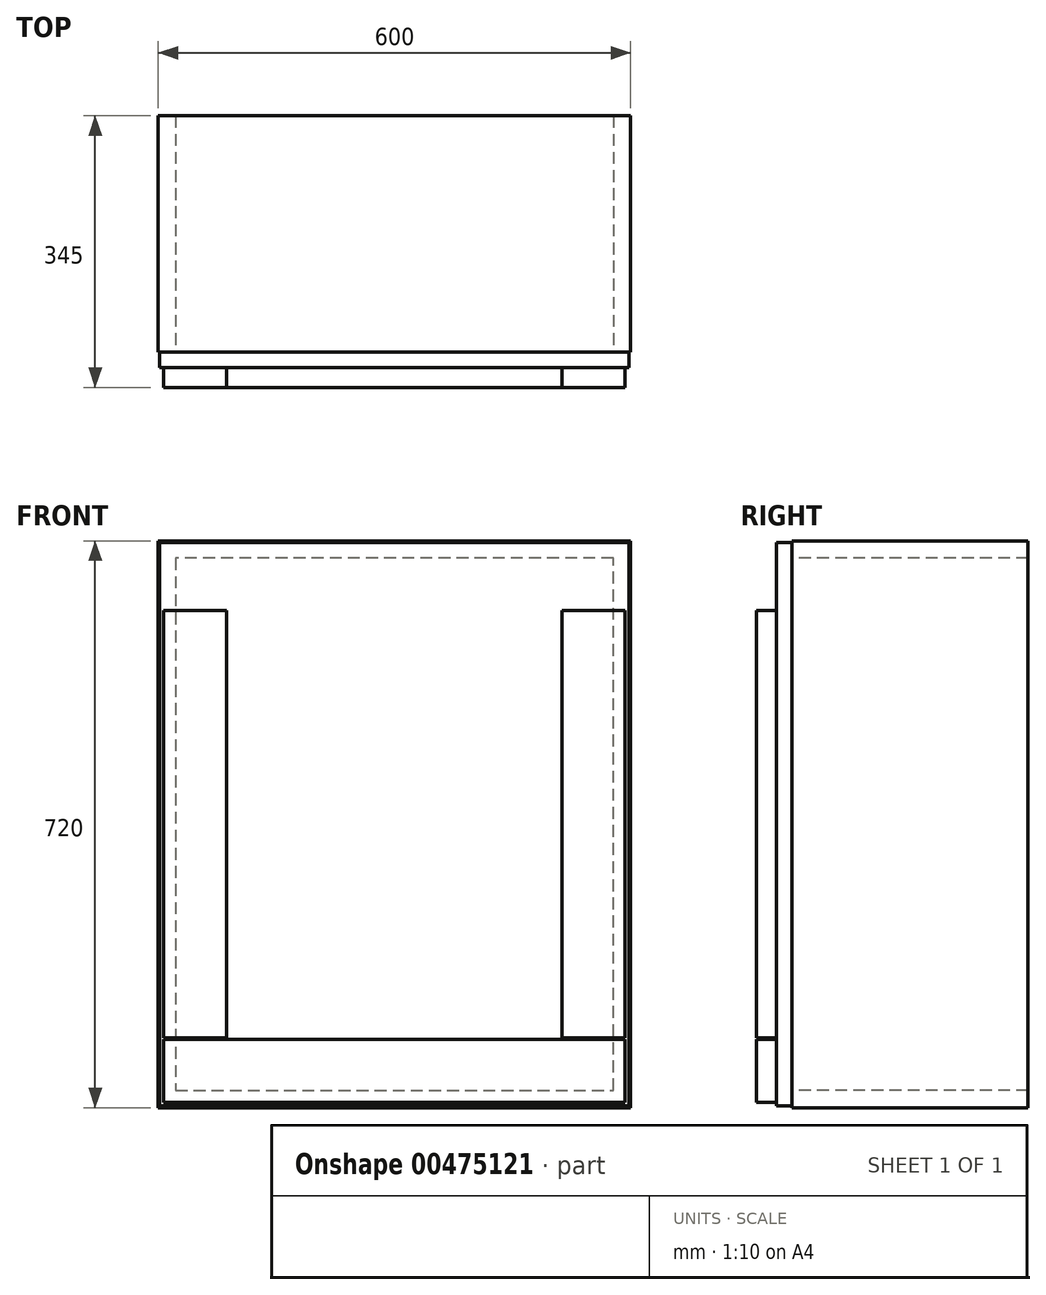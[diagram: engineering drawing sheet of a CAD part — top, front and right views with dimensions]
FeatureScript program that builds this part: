
annotation { "Feature Type Name" : "Feature", "Feature Type Description" : "" }
export const myFeature = defineFeature(function(context is Context, id is Id, definition is map)
    precondition{}
    {
        {
            var Q0;
            Q0=qCreatedBy(makeId("Top.planeOp"),FACE);
            var sketch = newSketch(context, id + "F0", { "sketchPlane" : qUnion([Q0])});
            skLineSegment(sketch, "E0.bottom", {"start": v(-300, 150) * mm, "end": v(300, 150) * mm});
            skLineSegment(sketch, "E0.top", {"start": v(-300, -150) * mm, "end": v(300, -150) * mm});
            skLineSegment(sketch, "E0.left", {"start": v(-300, 150) * mm, "end": v(-300, -150) * mm});
            skLineSegment(sketch, "E0.right", {"start": v(300, 150) * mm, "end": v(300, -150) * mm});
            skPoint(sketch, "E0.middle", {"position": v(0, 0) * mm});
            skSolve(sketch);
        }
        {
            var Q0;
            Q0=qSketchRegion(id+"F0",true);
            extrude(context, id + "F1", {"entities" : qUnion([Q0]), "depth" : 720 * mm, "offsetDistance" : 25 * mm});
        }
        {
            var Q0;
            Q0=makeQuery(id+"F1.opExtrude","SWEPT_FACE",FACE,{"disambiguationData":[OSD([sQuery(id+"F0.wireOp",EDGE,"E0.top")])]});
            var sketch = newSketch(context, id + "F2", { "sketchPlane" : qUnion([Q0])});
            skLineSegment(sketch, "E1.0", {"start": v(-278, 22) * mm, "end": v(278, 22) * mm});
            skLineSegment(sketch, "E1.1", {"start": v(-278, 698) * mm, "end": v(-278, 22) * mm});
            skLineSegment(sketch, "E1.2", {"start": v(278, 698) * mm, "end": v(-278, 698) * mm});
            skLineSegment(sketch, "E1.3", {"start": v(278, 22) * mm, "end": v(278, 698) * mm});
            skSolve(sketch);
        }
        {
            var Q0;
            Q0=makeQuery(id+"F2.imprint","IMPRINT",FACE,{"disambiguationData":[TD([[makeQuery(id+"F2.imprint","IMPRINT",EDGE,{"derivedFrom":sQuery(id+"F2.wireOp",EDGE,"E1.0")}),1.0]])]});
            extrude(context, id + "F3", {"entities" : qUnion([Q0]), "operationType" : NewBodyOperationType.REMOVE, "endBound" : BoundingType.UP_TO_NEXT, "oppositeDirection" : true, "depth" : 25 * mm, "offsetDistance" : 25 * mm});
        }
        {
            var Q0;
            Q0=makeQuery(id+"F1.opExtrude","SWEPT_FACE",FACE,{"disambiguationData":[OSD([sQuery(id+"F0.wireOp",EDGE,"E0.top")])]});
            var sketch = newSketch(context, id + "F4", { "sketchPlane" : qUnion([Q0])});
            skLineSegment(sketch, "E2.0", {"start": v(-298, 718) * mm, "end": v(298, 718) * mm});
            skLineSegment(sketch, "E2.1", {"start": v(-298, 718) * mm, "end": v(-298, 2) * mm});
            skLineSegment(sketch, "E2.2", {"start": v(-298, 2) * mm, "end": v(298, 2) * mm});
            skLineSegment(sketch, "E2.3", {"start": v(298, 718) * mm, "end": v(298, 2) * mm});
            skSolve(sketch);
        }
        {
            var Q0;
            Q0=qSketchRegion(id+"F4",true);
            extrude(context, id + "F5", {"entities" : qUnion([Q0]), "operationType" : NewBodyOperationType.ADD, "depth" : 20 * mm, "offsetDistance" : 25 * mm});
        }
        {
            var Q0;
            Q0=makeQuery(id+"F5.opExtrude","CAP_FACE",FACE,{"disambiguationData":[OSD([sQuery(id+"F4.wireOp",EDGE,"E2.0"),sQuery(id+"F4.wireOp",EDGE,"E2.1"),sQuery(id+"F4.wireOp",EDGE,"E2.2"),sQuery(id+"F4.wireOp",EDGE,"E2.3")])],"isStart":false});
            var sketch = newSketch(context, id + "F6", { "sketchPlane" : qUnion([Q0])});
            skLineSegment(sketch, "E3.0", {"start": v(293, 7) * mm, "end": v(293, 713) * mm});
            skLineSegment(sketch, "E3.1", {"start": v(-293, 7) * mm, "end": v(293, 7) * mm});
            skLineSegment(sketch, "E3.2", {"start": v(-293, 713) * mm, "end": v(-293, 7) * mm});
            skLineSegment(sketch, "E3.3", {"start": v(293, 713) * mm, "end": v(-293, 713) * mm});
            skLineSegment(sketch, "E4.bottom", {"start": v(-293, 713) * mm, "end": v(293, 713) * mm});
            skLineSegment(sketch, "E4.top", {"start": v(-293, 633) * mm, "end": v(293, 633) * mm});
            skLineSegment(sketch, "E4.left", {"start": v(-293, 713) * mm, "end": v(-293, 633) * mm});
            skLineSegment(sketch, "E4.right", {"start": v(293, 713) * mm, "end": v(293, 633) * mm});
            skLineSegment(sketch, "E5.top", {"start": v(-293, 87) * mm, "end": v(293, 87) * mm});
            skLineSegment(sketch, "E5.left", {"start": v(-293, 7) * mm, "end": v(-293, 87) * mm});
            skLineSegment(sketch, "E5.right", {"start": v(293, 7) * mm, "end": v(293, 87) * mm});
            skLineSegment(sketch, "E6.bottom", {"start": v(213, 631.5) * mm, "end": v(293, 631.5) * mm});
            skLineSegment(sketch, "E6.top", {"start": v(213, 88.5) * mm, "end": v(293, 88.5) * mm});
            skLineSegment(sketch, "E6.left", {"start": v(213, 631.5) * mm, "end": v(213, 88.5) * mm});
            skLineSegment(sketch, "E6.right", {"start": v(293, 631.5) * mm, "end": v(293, 88.5) * mm});
            skLineSegment(sketch, "E7.bottom", {"start": v(-293, 88.5) * mm, "end": v(-213, 88.5) * mm});
            skLineSegment(sketch, "E7.top", {"start": v(-293, 631.5) * mm, "end": v(-213, 631.5) * mm});
            skLineSegment(sketch, "E7.left", {"start": v(-293, 88.5) * mm, "end": v(-293, 631.5) * mm});
            skLineSegment(sketch, "E7.right", {"start": v(-213, 88.5) * mm, "end": v(-213, 631.5) * mm});
            skSolve(sketch);
        }
        {
            var Q0;
            Q0=makeQuery(id+"F6.imprint","IMPRINT",FACE,{"disambiguationData":[TD([[makeQuery(id+"F6.imprint","IMPRINT",EDGE,{"derivedFrom":sQuery(id+"F6.wireOp",EDGE,"E4.bottom")}),-1.0]])]});
            var Q1;
            Q1=makeQuery(id+"F6.imprint","IMPRINT",FACE,{"disambiguationData":[TD([[makeQuery(id+"F6.imprint","IMPRINT",EDGE,{"derivedFrom":sQuery(id+"F6.wireOp",EDGE,"E7.bottom")}),1.0]])]});
            var Q2;
            Q2=makeQuery(id+"F6.imprint","IMPRINT",FACE,{"disambiguationData":[TD([[makeQuery(id+"F6.imprint","IMPRINT",EDGE,{"derivedFrom":sQuery(id+"F6.wireOp",EDGE,"E6.bottom")}),-1.0]])]});
            var Q3;
            Q3=makeQuery(id+"F6.imprint","IMPRINT",FACE,{"disambiguationData":[TD([[makeQuery(id+"F6.imprint","IMPRINT",EDGE,{"derivedFrom":sQuery(id+"F6.wireOp",EDGE,"E3.1")}),1.0]])]});
            extrude(context, id + "F7", {"entities" : qUnion([Q0, Q1, Q2, Q3]), "operationType" : NewBodyOperationType.ADD, "depth" : 25 * mm, "offsetDistance" : 25 * mm});
        }
    });
